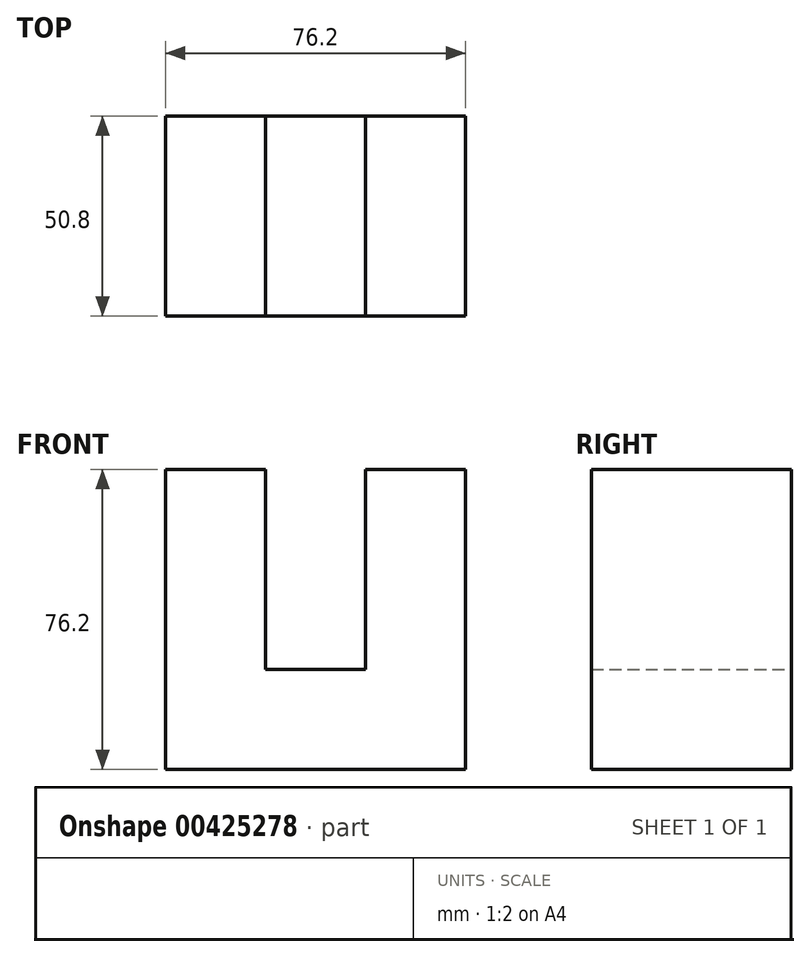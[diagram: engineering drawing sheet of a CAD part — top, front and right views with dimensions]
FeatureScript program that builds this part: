
annotation { "Feature Type Name" : "Feature", "Feature Type Description" : "" }
export const myFeature = defineFeature(function(context is Context, id is Id, definition is map)
    precondition{}
    {
        {
            var Q0;
            Q0=qCreatedBy(makeId("Front.planeOp"),FACE);
            var sketch = newSketch(context, id + "F0", { "sketchPlane" : qUnion([Q0])});
            skLineSegment(sketch, "E0", {"start": v(12.42, 76.2) * mm, "end": v(-12.98, 76.2) * mm});
            skLineSegment(sketch, "E1", {"start": v(-12.98, 76.2) * mm, "end": v(-12.98, 0) * mm});
            skLineSegment(sketch, "E2", {"start": v(-12.98, 0) * mm, "end": v(63.22, 0) * mm});
            skLineSegment(sketch, "E3", {"start": v(63.22, 0) * mm, "end": v(63.22, 76.2) * mm});
            skLineSegment(sketch, "E4", {"start": v(12.42, 76.2) * mm, "end": v(12.42, 25.4) * mm});
            skLineSegment(sketch, "E5", {"start": v(63.22, 76.2) * mm, "end": v(37.82, 76.2) * mm});
            skLineSegment(sketch, "E6", {"start": v(37.82, 76.2) * mm, "end": v(37.82, 25.4) * mm});
            skLineSegment(sketch, "E7", {"start": v(12.42, 25.4) * mm, "end": v(37.82, 25.4) * mm});
            skSolve(sketch);
        }
        {
            var Q0;
            Q0 = qSketchRegion(id + "F0", true);
            extrude(context, id + "F1", {"entities" : qUnion([Q0]), "depth" : 50.8 * mm});
        }
    });
